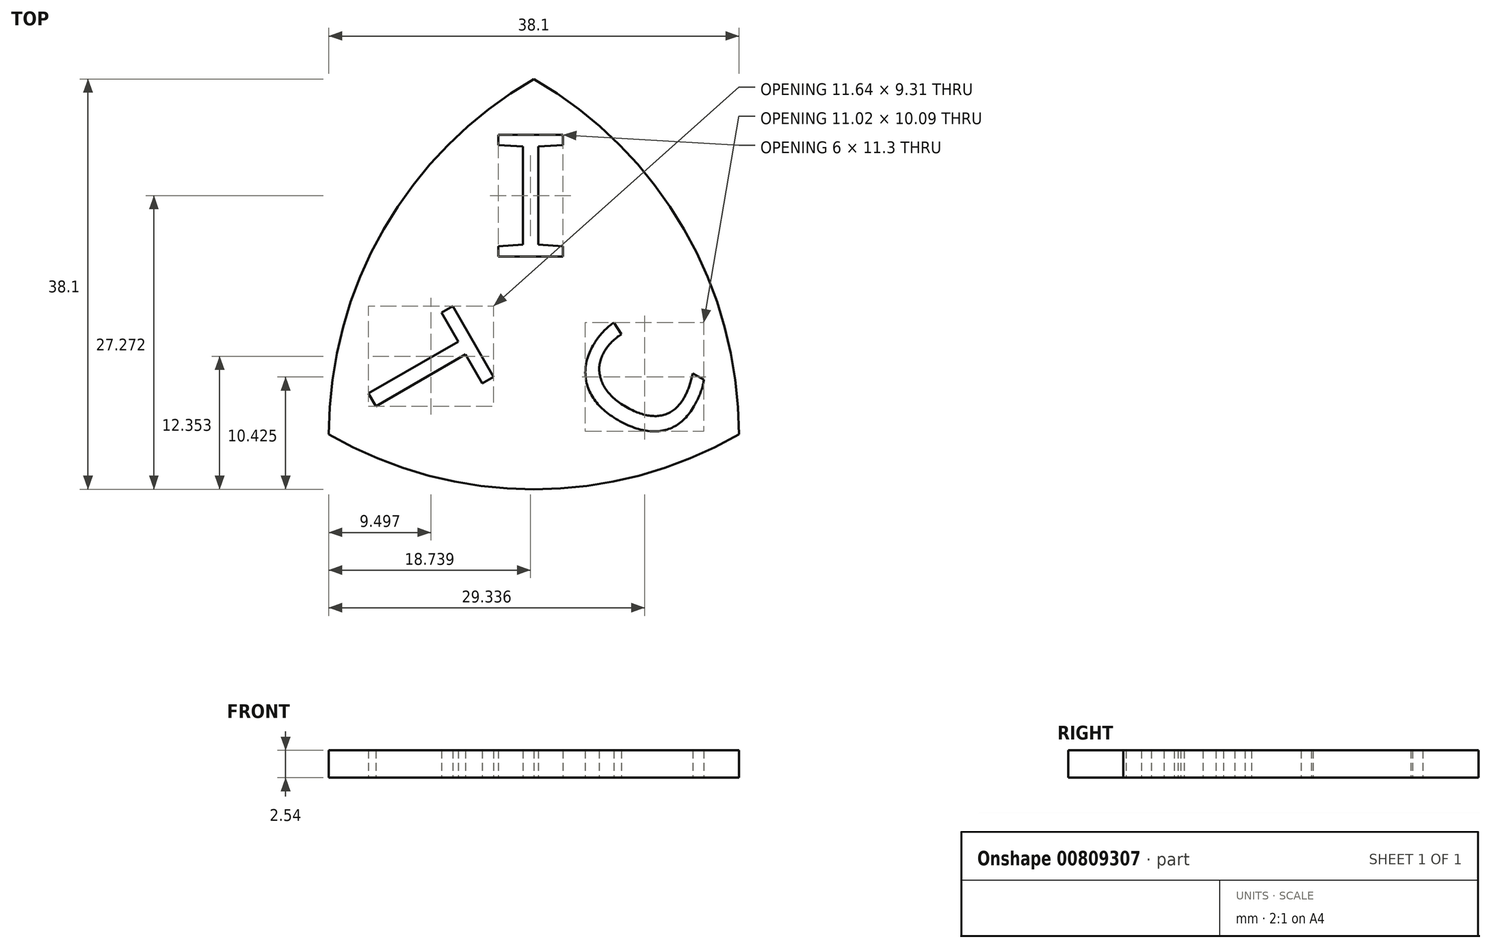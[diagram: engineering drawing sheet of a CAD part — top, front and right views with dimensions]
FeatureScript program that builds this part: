
annotation { "Feature Type Name" : "Feature", "Feature Type Description" : "" }
export const myFeature = defineFeature(function(context is Context, id is Id, definition is map)
    precondition{}
    {
        {
            var Q0;
            Q0=qCreatedBy(makeId("Top.planeOp"),FACE);
            var sketch = newSketch(context, id + "F0", { "sketchPlane" : qUnion([Q0])});
            skCircle(sketch, "E0", {"center": v(0, 0) * mm, "radius": 38.1 * mm});
            skSolve(sketch);
        }
        {
            var Q0;
            Q0=qCreatedBy(makeId("Top.planeOp"),FACE);
            var sketch = newSketch(context, id + "F1", { "sketchPlane" : qUnion([Q0])});
            skCircle(sketch, "E1", {"center": v(-38.1, 0) * mm, "radius": 38.1 * mm});
            skSolve(sketch);
        }
        {
            var Q0;
            Q0=qCreatedBy(makeId("Top.planeOp"),FACE);
            var sketch = newSketch(context, id + "F2", { "sketchPlane" : qUnion([Q0])});
            skCircle(sketch, "E2", {"center": v(-19.05, 33) * mm, "radius": 38.1 * mm});
            skSolve(sketch);
        }
        {
            var Q0;
            Q0=makeQuery(id+"F0.imprint","IMPRINT",FACE,{"disambiguationData":[TD([[makeQuery(id+"F0.imprint","IMPRINT",EDGE,{"derivedFrom":sQuery(id+"F0.wireOp",EDGE,"E0")}),1.0]])]});
            extrude(context, id + "F3", {"entities" : qUnion([Q0]), "depth" : 2.54 * mm, "offsetDistance" : 25.4 * mm});
        }
        {
            var Q0;
            Q0=makeQuery(id+"F2.imprint","IMPRINT",FACE,{"disambiguationData":[TD([[makeQuery(id+"F2.imprint","IMPRINT",EDGE,{"derivedFrom":sQuery(id+"F2.wireOp",EDGE,"E2")}),1.0]])]});
            extrude(context, id + "F4", {"entities" : qUnion([Q0]), "depth" : 2.54 * mm, "offsetDistance" : 25.4 * mm});
        }
        {
            var Q0;
            Q0=makeQuery(id+"F1.imprint","IMPRINT",FACE,{"disambiguationData":[TD([[makeQuery(id+"F1.imprint","IMPRINT",EDGE,{"derivedFrom":sQuery(id+"F1.wireOp",EDGE,"E1")}),1.0]])]});
            extrude(context, id + "F5", {"entities" : qUnion([Q0]), "depth" : 2.54 * mm, "offsetDistance" : 25.4 * mm});
        }
        {
            var Q0;
            Q0=makeQuery(id+"F3.opExtrude","SWEPT_BODY",BODY,{"disambiguationData":[OSD([sQuery(id+"F0.wireOp",EDGE,"E0")])]});
            var Q1;
            Q1=makeQuery(id+"F4.opExtrude","SWEPT_BODY",BODY,{"disambiguationData":[OSD([sQuery(id+"F2.wireOp",EDGE,"E2")])]});
            var Q2;
            Q2=makeQuery(id+"F5.opExtrude","SWEPT_BODY",BODY,{"disambiguationData":[OSD([sQuery(id+"F1.wireOp",EDGE,"E1")])]});
            booleanBodies(context, id + "F6", {"operationType" : BooleanOperationType.INTERSECTION, "tools" : qUnion([Q0, Q1, Q2])});
        }
        {
            var Q0;
            Q0=qCreatedBy(makeId("Top.planeOp"),FACE);
            var sketch = newSketch(context, id + "F7", { "sketchPlane" : qUnion([Q0])});
            skText(sketch, "E3", { "text": "C", "fontName": "DroidSansMono.ttf"});
            skText(sketch, "E4", { "text": "I", "fontName": "DroidSansMono.ttf"});
            skText(sketch, "E5", { "text": "T", "fontName": "DroidSansMono.ttf"});
            const initialGuessF7  = {"E3": [-0.0071, -0.00215, 0.5, 0.86603, 0.01073], "E4": [-0.0241, 0.01652, 1, 0, 0.0114], "E5": [-0.03635, 0.00714, 0.5, -0.86603, 0.01094]};
            skSetInitialGuess(sketch, initialGuessF7);
            skSolve(sketch);
        }
        {
            var Q0;
            Q0 = qSketchRegion(id + "F7", true);
            extrude(context, id + "F8", {"entities" : qUnion([Q0]), "depth" : 2.54 * mm, "offsetDistance" : 25.4 * mm});
        }
        {
            var Q0;
            Q0=makeQuery(id+"F8.opExtrude","SWEPT_BODY",BODY,{"disambiguationData":[OSD([sQuery(id+"F7.wireOp",EDGE,"E5.sketch_text.stroke-0"),sQuery(id+"F7.wireOp",EDGE,"E5.sketch_text.stroke-1"),sQuery(id+"F7.wireOp",EDGE,"E5.sketch_text.stroke-2"),sQuery(id+"F7.wireOp",EDGE,"E5.sketch_text.stroke-3"),sQuery(id+"F7.wireOp",EDGE,"E5.sketch_text.stroke-4"),sQuery(id+"F7.wireOp",EDGE,"E5.sketch_text.stroke-5"),sQuery(id+"F7.wireOp",EDGE,"E5.sketch_text.stroke-6"),sQuery(id+"F7.wireOp",EDGE,"E5.sketch_text.stroke-7")])]});
            var Q1;
            Q1=makeQuery(id+"F8.opExtrude","SWEPT_BODY",BODY,{"disambiguationData":[OSD([sQuery(id+"F7.wireOp",EDGE,"E3.sketch_text.stroke-0"),sQuery(id+"F7.wireOp",EDGE,"E3.sketch_text.stroke-1"),sQuery(id+"F7.wireOp",EDGE,"E3.sketch_text.stroke-2"),sQuery(id+"F7.wireOp",EDGE,"E3.sketch_text.stroke-3"),sQuery(id+"F7.wireOp",EDGE,"E3.sketch_text.stroke-4"),sQuery(id+"F7.wireOp",EDGE,"E3.sketch_text.stroke-5"),sQuery(id+"F7.wireOp",EDGE,"E3.sketch_text.stroke-6"),sQuery(id+"F7.wireOp",EDGE,"E3.sketch_text.stroke-7"),sQuery(id+"F7.wireOp",EDGE,"E3.sketch_text.stroke-8"),sQuery(id+"F7.wireOp",EDGE,"E3.sketch_text.stroke-9"),sQuery(id+"F7.wireOp",EDGE,"E3.sketch_text.stroke-10"),sQuery(id+"F7.wireOp",EDGE,"E3.sketch_text.stroke-11"),sQuery(id+"F7.wireOp",EDGE,"E3.sketch_text.stroke-12"),sQuery(id+"F7.wireOp",EDGE,"E3.sketch_text.stroke-13")])]});
            var Q2;
            Q2=makeQuery(id+"F8.opExtrude","SWEPT_BODY",BODY,{"disambiguationData":[OSD([sQuery(id+"F7.wireOp",EDGE,"E4.sketch_text.stroke-0"),sQuery(id+"F7.wireOp",EDGE,"E4.sketch_text.stroke-1"),sQuery(id+"F7.wireOp",EDGE,"E4.sketch_text.stroke-2"),sQuery(id+"F7.wireOp",EDGE,"E4.sketch_text.stroke-3"),sQuery(id+"F7.wireOp",EDGE,"E4.sketch_text.stroke-4"),sQuery(id+"F7.wireOp",EDGE,"E4.sketch_text.stroke-5"),sQuery(id+"F7.wireOp",EDGE,"E4.sketch_text.stroke-6"),sQuery(id+"F7.wireOp",EDGE,"E4.sketch_text.stroke-7"),sQuery(id+"F7.wireOp",EDGE,"E4.sketch_text.stroke-8"),sQuery(id+"F7.wireOp",EDGE,"E4.sketch_text.stroke-9"),sQuery(id+"F7.wireOp",EDGE,"E4.sketch_text.stroke-10"),sQuery(id+"F7.wireOp",EDGE,"E4.sketch_text.stroke-11")])]});
            var Q3;
            Q3=makeQuery(id+"F6.opBoolean","INTERSECT",BODY,{"derivedFrom":[makeQuery(id+"F3.opExtrude","SWEPT_BODY",BODY,{"disambiguationData":[OSD([sQuery(id+"F0.wireOp",EDGE,"E0")])]}),makeQuery(id+"F4.opExtrude","SWEPT_BODY",BODY,{"disambiguationData":[OSD([sQuery(id+"F2.wireOp",EDGE,"E2")])]}),makeQuery(id+"F5.opExtrude","SWEPT_BODY",BODY,{"disambiguationData":[OSD([sQuery(id+"F1.wireOp",EDGE,"E1")])]})]});
            booleanBodies(context, id + "F9", {"operationType" : BooleanOperationType.SUBTRACTION, "tools" : qUnion([Q0, Q1, Q2]), "targets" : qUnion([Q3])});
        }
    });
